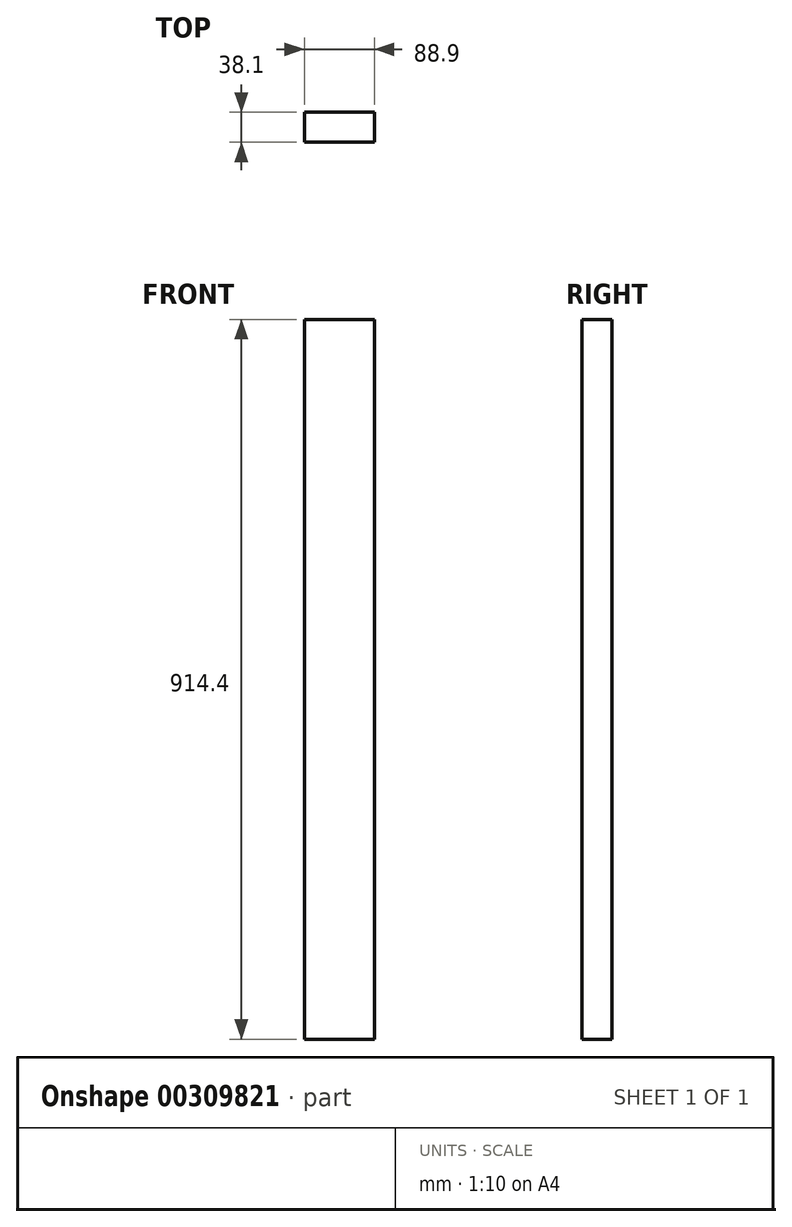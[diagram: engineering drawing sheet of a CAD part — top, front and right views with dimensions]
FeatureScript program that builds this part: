
annotation { "Feature Type Name" : "Feature", "Feature Type Description" : "" }
export const myFeature = defineFeature(function(context is Context, id is Id, definition is map)
    precondition{}
    {
        {
            var Q0;
            Q0=qCreatedBy(makeId("Front.planeOp"),FACE);
            var sketch = newSketch(context, id + "F0", { "sketchPlane" : qUnion([Q0])});
            skLineSegment(sketch, "E0.bottom", {"start": v(44.45, 457.2) * mm, "end": v(-44.45, 457.2) * mm});
            skLineSegment(sketch, "E0.top", {"start": v(44.45, -457.2) * mm, "end": v(-44.45, -457.2) * mm});
            skLineSegment(sketch, "E0.left", {"start": v(44.45, 457.2) * mm, "end": v(44.45, -457.2) * mm});
            skLineSegment(sketch, "E0.right", {"start": v(-44.45, 457.2) * mm, "end": v(-44.45, -457.2) * mm});
            skPoint(sketch, "E0.middle", {"position": v(0, 0) * mm});
            skSolve(sketch);
        }
        {
            var Q0;
            Q0 = qSketchRegion(id + "F0", true);
            extrude(context, id + "F1", {"entities" : qUnion([Q0]), "depth" : 38.1 * mm});
        }
    });
